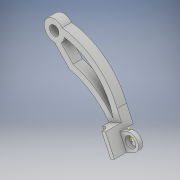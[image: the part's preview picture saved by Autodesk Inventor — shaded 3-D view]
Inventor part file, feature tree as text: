
AUTODESK INVENTOR PART (.ipt)
format: ipt  version: 2018 (Build 220112000, 112)  size: 207,360 bytes
history: native  units: in
note: dims shown in document units (in); Inventor stores cm internally (conversion verified against a paired STEP export)
features: sketch x10, extrude x6, plane x1, fillet x1
ambient origin geometry x8: Origin, YZ Plane, XZ Plane, XY Plane, X Axis, Y Axis, Z Axis, Center Point
bodies: Solid1 (feature_tree)
feature tree (18):
  sketch  "Sketch1"  dims[d15=1.0in d47=0.1969in d48=0.1969in]
  extrude  "Extrusion12"  Depth=0.1969in
  sketch  "Sketch16"  dims[d63=2.1654in d64=0.1969in]
  extrude  "Extrusion16"  Depth=0.1969in
  extrude  "Extrusion19"  Depth=0.1969in
  plane  "Work Plane9"
  sketch  "Sketch25"  dims[d75=0.2756in d76=0.2756in d77=0.0in]
  sketch  "Sketch26"  dims[d101=0.1181in d102=0.3937in d103=0.0in d106=0.5906in]
  extrude  "Extrusion20"  Depth=0.1969in
  sketch  "Sketch30"  dims[d116=0.1575in d117=0.0in]
  extrude  "Extrusion21"  Depth=0.2756in TaperAngle=0.0deg
  extrude  "Extrusion22"  Depth=0.3937in TaperAngle=0.0deg
  fillet  "Fillet5"  Radius=0.5906in
  sketch  "Sketch19"  dims[d65=0.1969in d66=0.7874in]
  sketch  "Sketch24"  dims[d68=0.1969in d74=0.1969in]
  sketch  "Sketch27"  dims[d115=0.5906in]
  sketch  "Sketch31"  dims[d118=0.4724in]
  sketch  "Sketch32"  dims[d119=0.1181in d120=0.374in d121=0.2165in d122=0.2362in d123=0.4724in d124=0.0in d129=0.2362in d130=0.1181in d131=0.2362in d132=0.1181in d133=0.4724in d134=0.0in d135=0.1516in d136=0.0in d139=0.2362in d140=0.315in d141=0.1181in d142=0.0in d143=0.2362in]
